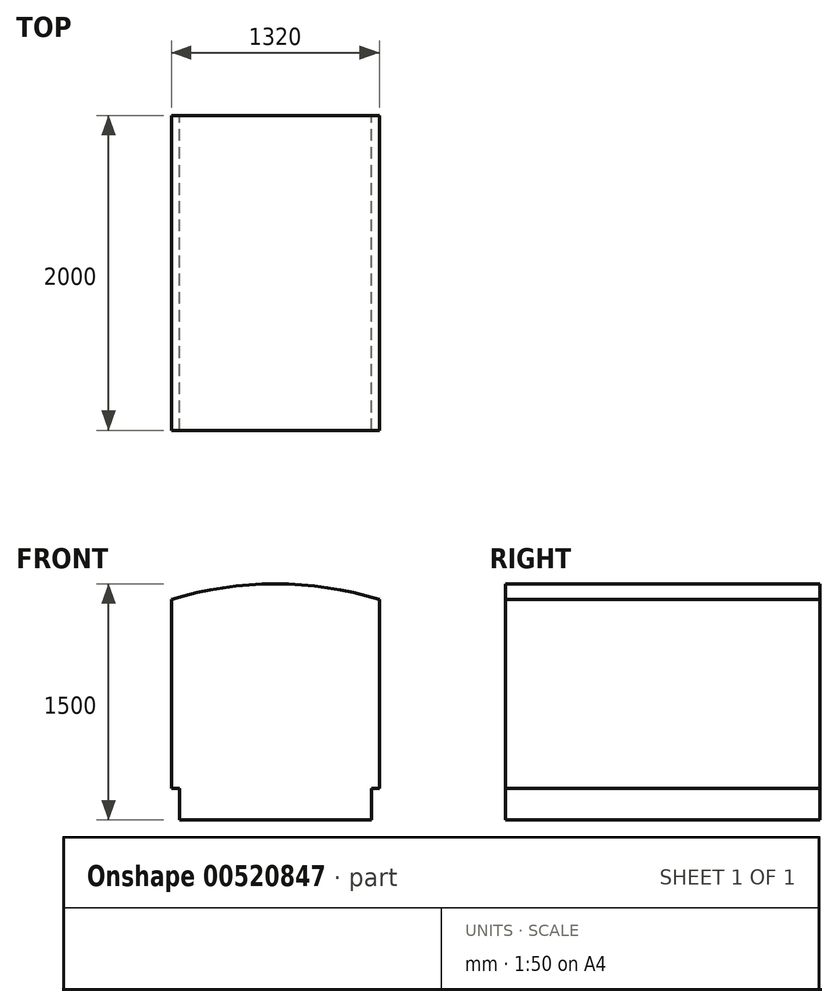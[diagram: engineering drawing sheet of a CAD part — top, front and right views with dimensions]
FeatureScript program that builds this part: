
annotation { "Feature Type Name" : "Feature", "Feature Type Description" : "" }
export const myFeature = defineFeature(function(context is Context, id is Id, definition is map)
    precondition{}
    {
        {
            var Q0;
            Q0=qCreatedBy(makeId("Front.planeOp"),FACE);
            var sketch = newSketch(context, id + "F0", { "sketchPlane" : qUnion([Q0])});
            skLineSegment(sketch, "E0", {"start": v(-610, 0) * mm, "end": v(610, 0) * mm});
            skLineSegment(sketch, "E1", {"start": v(-610, 0) * mm, "end": v(-610, 200) * mm});
            skLineSegment(sketch, "E2", {"start": v(610, 0) * mm, "end": v(610, 200) * mm});
            skLineSegment(sketch, "E3", {"start": v(610, 200) * mm, "end": v(660, 200) * mm});
            skLineSegment(sketch, "E4", {"start": v(-610, 200) * mm, "end": v(-660, 200) * mm});
            skLineSegment(sketch, "E5", {"start": v(-660, 200) * mm, "end": v(-660, 1400) * mm});
            skLineSegment(sketch, "E6", {"start": v(660, 200) * mm, "end": v(660, 1400) * mm});
            skLineSegment(sketch, "E7", {"start": v(660, 1400) * mm, "end": v(-660, 1400) * mm, "construction": true});
            skArc(sketch, "E8", {"start": v(660, 1400) * mm, "mid": v(0, 1500) * mm, "end": v(-660, 1400) * mm});
            skSolve(sketch);
        }
        {
            var Q0;
            Q0=makeQuery(id+"F0.imprint","IMPRINT",FACE,{"disambiguationData":[TD([[makeQuery(id+"F0.imprint","IMPRINT",EDGE,{"derivedFrom":sQuery(id+"F0.wireOp",EDGE,"E0")}),1.0]])]});
            extrude(context, id + "F1", {"entities" : qUnion([Q0]), "depth" : 2000 * mm, "offsetDistance" : 25 * mm});
        }
    });
